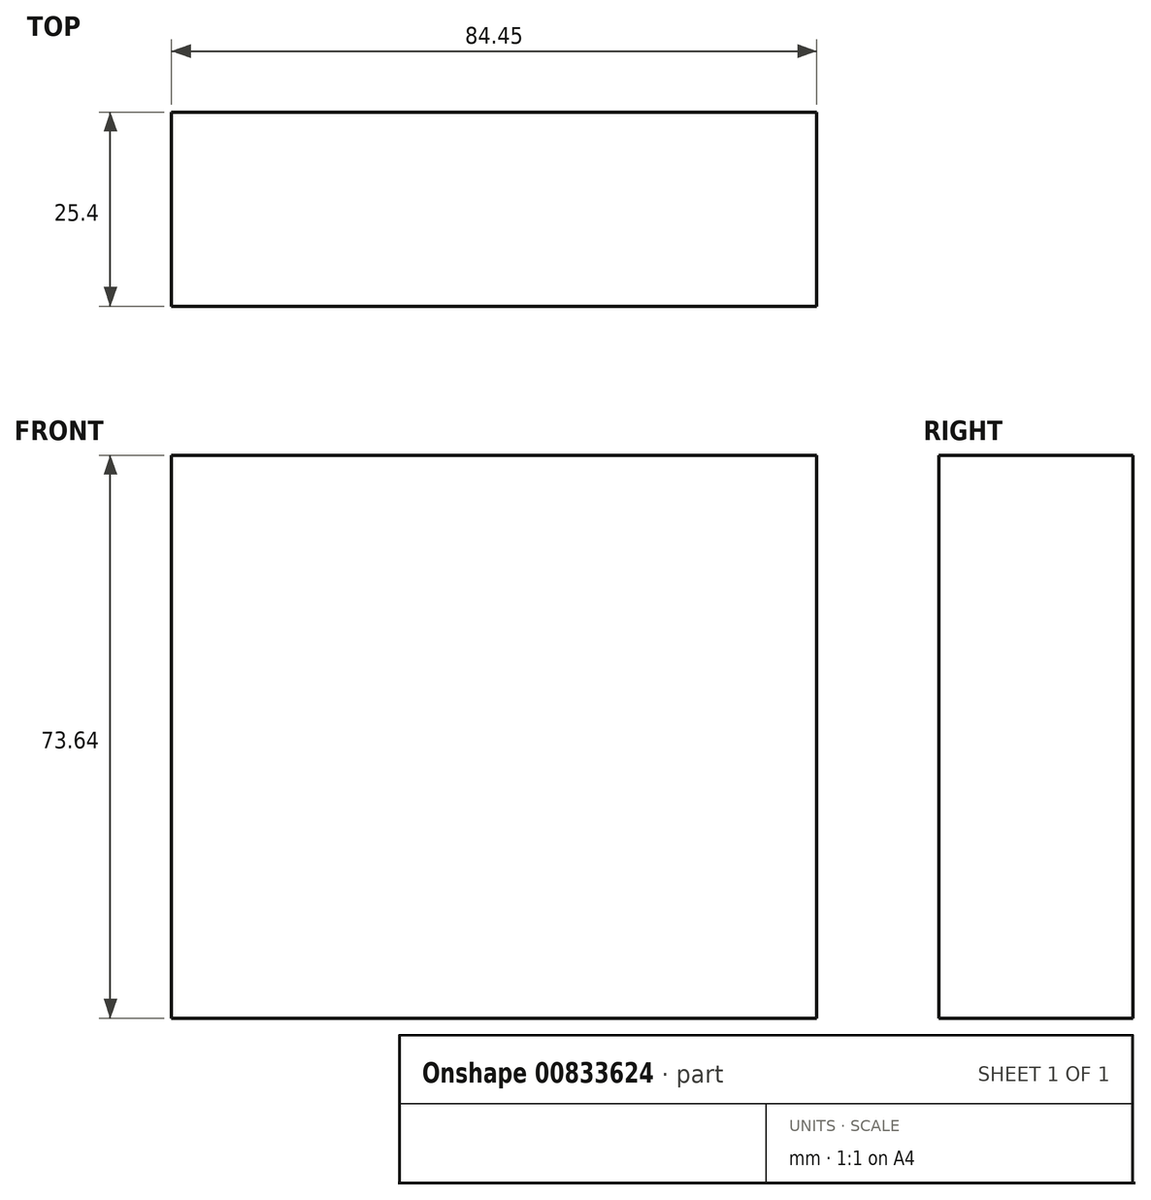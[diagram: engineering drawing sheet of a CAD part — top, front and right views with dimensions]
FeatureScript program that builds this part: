
annotation { "Feature Type Name" : "Feature", "Feature Type Description" : "" }
export const myFeature = defineFeature(function(context is Context, id is Id, definition is map)
    precondition{}
    {
        {
            var Q0;
            Q0=qCreatedBy(makeId("Front.planeOp"),FACE);
            var sketch = newSketch(context, id + "F0", { "sketchPlane" : qUnion([Q0])});
            skLineSegment(sketch, "E0.bottom", {"start": v(-59.18, 45.49) * mm, "end": v(25.27, 45.49) * mm});
            skLineSegment(sketch, "E0.top", {"start": v(-59.18, -28.15) * mm, "end": v(25.27, -28.15) * mm});
            skLineSegment(sketch, "E0.left", {"start": v(-59.18, 45.49) * mm, "end": v(-59.18, -28.15) * mm});
            skLineSegment(sketch, "E0.right", {"start": v(25.27, 45.49) * mm, "end": v(25.27, -28.15) * mm});
            skSolve(sketch);
        }
        {
            var Q0;
            Q0 = qSketchRegion(id + "F0", true);
            extrude(context, id + "F1", {"entities" : qUnion([Q0]), "depth" : 25.4 * mm, "offsetDistance" : 25.4 * mm});
        }
        {
            var Q0;
            Q0=makeQuery(id+"F1.opExtrude","CAP_FACE",FACE,{"disambiguationData":[OSD([sQuery(id+"F0.wireOp",EDGE,"E0.bottom"),sQuery(id+"F0.wireOp",EDGE,"E0.top"),sQuery(id+"F0.wireOp",EDGE,"E0.left"),sQuery(id+"F0.wireOp",EDGE,"E0.right")])],"isStart":false});
            var sketch = newSketch(context, id + "F2", { "sketchPlane" : qUnion([Q0])});
            skCircle(sketch, "E1", {"center": v(-41.12, 25.08) * mm, "radius": 19.4 * mm});
            skCircle(sketch, "E2", {"center": v(-23.88, 33.98) * mm, "radius": 27 * mm});
            skCircle(sketch, "E3", {"center": v(-23.88, 33.98) * mm, "radius": 24.32 * mm});
            skSolve(sketch);
        }
        {
            var Q0;
            Q0=sQuery(id+"F2.wireOp",EDGE,"E3");
            extrude(context, id + "F3", {"bodyType" : ToolBodyType.SURFACE, "surfaceEntities" : qUnion([Q0]), "depth" : 25.4 * mm, "offsetDistance" : 25.4 * mm});
        }
    });
